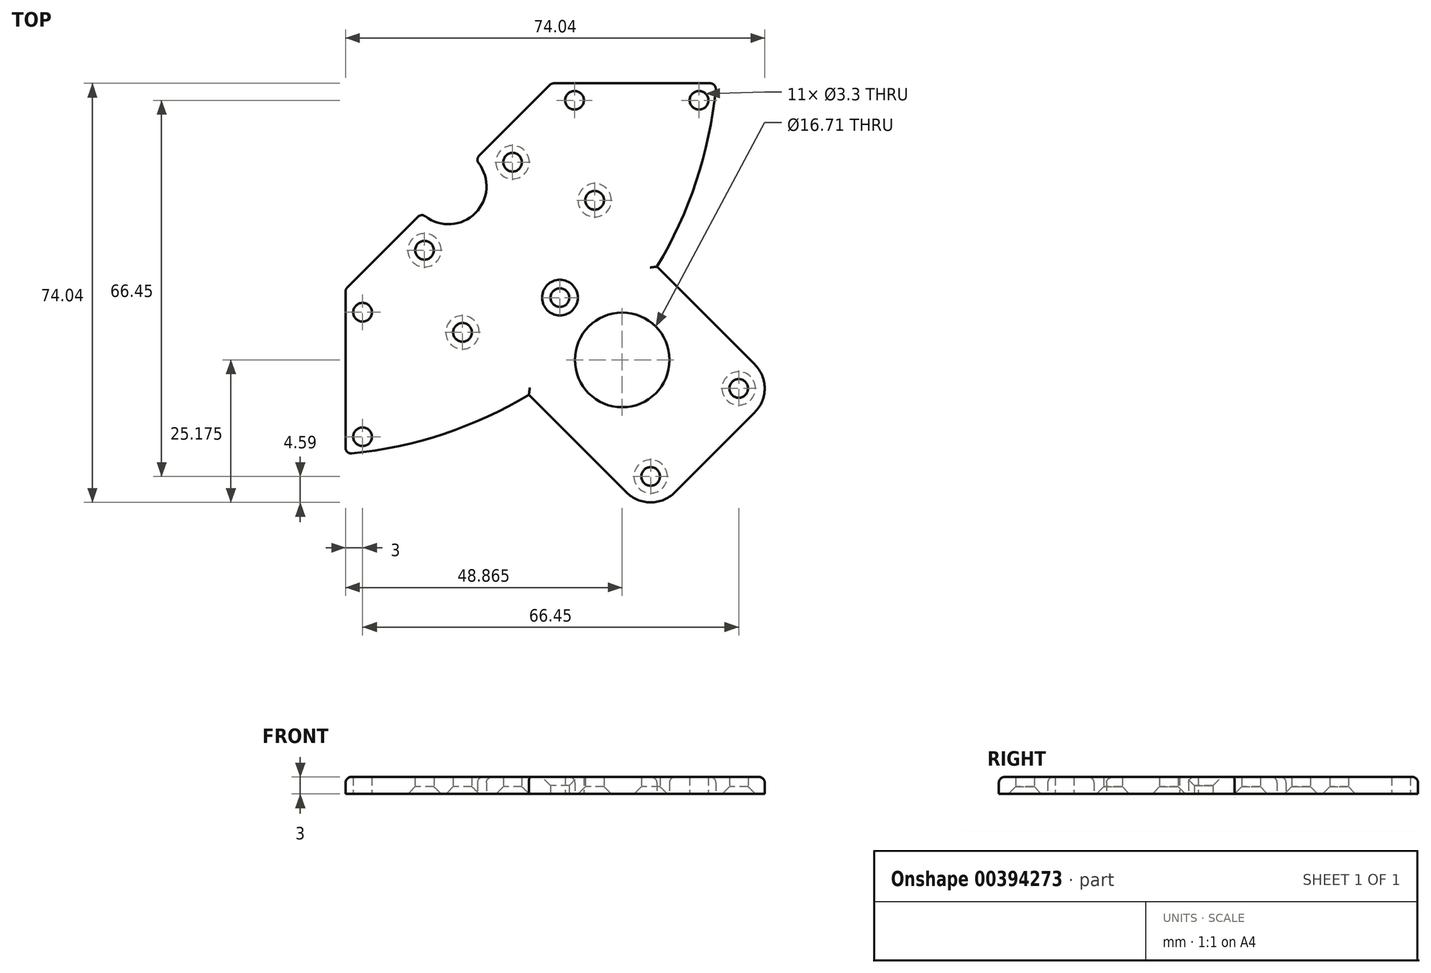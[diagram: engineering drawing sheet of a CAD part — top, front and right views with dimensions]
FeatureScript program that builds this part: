
annotation { "Feature Type Name" : "Feature", "Feature Type Description" : "" }
export const myFeature = defineFeature(function(context is Context, id is Id, definition is map)
    precondition{}
    {
        {
            var Q0;
            Q0=qCreatedBy(makeId("Top.planeOp"),FACE);
            var sketch = newSketch(context, id + "F0", { "sketchPlane" : qUnion([Q0])});
            skCircle(sketch, "E0", {"center": v(49, -11.56) * mm, "radius": 1.65 * mm});
            skCircle(sketch, "E1", {"center": v(71, -11.56) * mm, "radius": 1.65 * mm});
            skLineSegment(sketch, "E2", {"start": v(0, 0) * mm, "end": v(89.43, -89.43) * mm, "construction": true});
            skLineSegment(sketch, "E3", {"start": v(49, -11.56) * mm, "end": v(12.94, -47.62) * mm, "construction": true});
            skCircle(sketch, "E4", {"center": v(38.06, -22.5) * mm, "radius": 1.65 * mm});
            skCircle(sketch, "E5", {"center": v(78, -62.45) * mm, "radius": 1.65 * mm});
            skCircle(sketch, "E6", {"center": v(52.55, -29.22) * mm, "radius": 1.65 * mm});
            skArc(sketch, "E7", {"start": v(63.58, -40.95) * mm, "mid": v(70.67, -25.35) * mm, "end": v(74.06, -8.56) * mm});
            skLineSegment(sketch, "E8", {"start": v(73.77, -73.77) * mm, "end": v(85.08, -62.45) * mm});
            skLineSegment(sketch, "E9", {"start": v(85.08, -62.45) * mm, "end": v(63.58, -40.95) * mm});
            skLineSegment(sketch, "E10", {"start": v(31.49, -22) * mm, "end": v(44.93, -8.56) * mm});
            skLineSegment(sketch, "E11.trimOffspring", {"start": v(44.93, -8.56) * mm, "end": v(74.06, -8.56) * mm});
            skLineSegment(sketch, "E12.MirrorCS", {"start": v(8.56, -44.93) * mm, "end": v(8.56, -74.06) * mm});
            skLineSegment(sketch, "E13.MirrorCS", {"start": v(22, -31.49) * mm, "end": v(8.56, -44.93) * mm});
            skLineSegment(sketch, "E14.MirrorCS", {"start": v(62.45, -85.08) * mm, "end": v(40.95, -63.58) * mm});
            skLineSegment(sketch, "E15.MirrorCS", {"start": v(73.77, -73.77) * mm, "end": v(62.45, -85.08) * mm});
            skArc(sketch, "E16.MirrorCS", {"start": v(40.95, -63.58) * mm, "mid": v(25.35, -70.67) * mm, "end": v(8.56, -74.06) * mm});
            skCircle(sketch, "E17.MirrorC", {"center": v(29.22, -52.55) * mm, "radius": 1.65 * mm});
            skCircle(sketch, "E18.MirrorC", {"center": v(22.5, -38.06) * mm, "radius": 1.65 * mm});
            skCircle(sketch, "E19.MirrorC", {"center": v(11.56, -71) * mm, "radius": 1.65 * mm});
            skCircle(sketch, "E20.MirrorC", {"center": v(62.45, -78) * mm, "radius": 1.65 * mm});
            skCircle(sketch, "E21.MirrorC", {"center": v(11.56, -49) * mm, "radius": 1.65 * mm});
            skArc(sketch, "E22", {"start": v(22, -31.49) * mm, "mid": v(31.49, -31.49) * mm, "end": v(31.49, -22) * mm});
            skCircle(sketch, "E23", {"center": v(57.43, -57.43) * mm, "radius": 8.36 * mm});
            skCircle(sketch, "E24", {"center": v(46.42, -46.42) * mm, "radius": 1.65 * mm});
            skSolve(sketch);
        }
        {
            var Q0;
            Q0 = qSketchRegion(id + "F0", true);
            extrude(context, id + "F1", {"entities" : qUnion([Q0]), "depth" : 3 * mm});
        }
        {
            var Q0;
            Q0=makeQuery(id+"F1.opExtrude","CAP_EDGE",EDGE,{"disambiguationData":[OSD([sQuery(id+"F0.wireOp",EDGE,"E18.MirrorC")])],"isStart":true});
            var Q1;
            Q1=makeQuery(id+"F1.opExtrude","CAP_EDGE",EDGE,{"disambiguationData":[OSD([sQuery(id+"F0.wireOp",EDGE,"E17.MirrorC")])],"isStart":true});
            var Q2;
            Q2=makeQuery(id+"F1.opExtrude","CAP_EDGE",EDGE,{"disambiguationData":[OSD([sQuery(id+"F0.wireOp",EDGE,"E20.MirrorC")])],"isStart":true});
            var Q3;
            Q3=makeQuery(id+"F1.opExtrude","CAP_EDGE",EDGE,{"disambiguationData":[OSD([sQuery(id+"F0.wireOp",EDGE,"E5")])],"isStart":true});
            var Q4;
            Q4=makeQuery(id+"F1.opExtrude","CAP_EDGE",EDGE,{"disambiguationData":[OSD([sQuery(id+"F0.wireOp",EDGE,"E6")])],"isStart":true});
            var Q5;
            Q5=makeQuery(id+"F1.opExtrude","CAP_EDGE",EDGE,{"disambiguationData":[OSD([sQuery(id+"F0.wireOp",EDGE,"E4")])],"isStart":true});
            chamfer(context, id + "F2", {"entities" : qUnion([Q0, Q1, Q2, Q3, Q4, Q5]), "width" : 1.3 * mm, "tangentPropagation" : true});
        }
        {
            var Q0;
            Q0=makeQuery(id+"F1.opExtrude","CAP_EDGE",EDGE,{"disambiguationData":[OSD([sQuery(id+"F0.wireOp",EDGE,"E16.MirrorCS")])],"isStart":false});
            var Q1;
            Q1=makeQuery(id+"F1.opExtrude","CAP_EDGE",EDGE,{"disambiguationData":[OSD([sQuery(id+"F0.wireOp",EDGE,"E14.MirrorCS")])],"isStart":false});
            var Q2;
            Q2=makeQuery(id+"F1.opExtrude","CAP_EDGE",EDGE,{"disambiguationData":[OSD([sQuery(id+"F0.wireOp",EDGE,"E8"),sQuery(id+"F0.wireOp",EDGE,"E15.MirrorCS")])],"isStart":false});
            var Q3;
            Q3=makeQuery(id+"F1.opExtrude","CAP_EDGE",EDGE,{"disambiguationData":[OSD([sQuery(id+"F0.wireOp",EDGE,"E9")])],"isStart":false});
            var Q4;
            Q4=makeQuery(id+"F1.opExtrude","CAP_EDGE",EDGE,{"disambiguationData":[OSD([sQuery(id+"F0.wireOp",EDGE,"E7")])],"isStart":false});
            var Q5;
            Q5=makeQuery(id+"F1.opExtrude","CAP_EDGE",EDGE,{"disambiguationData":[OSD([sQuery(id+"F0.wireOp",EDGE,"E11.trimOffspring")])],"isStart":false});
            var Q6;
            Q6=makeQuery(id+"F1.opExtrude","CAP_EDGE",EDGE,{"disambiguationData":[OSD([sQuery(id+"F0.wireOp",EDGE,"E10")])],"isStart":false});
            var Q7;
            Q7=makeQuery(id+"F1.opExtrude","CAP_EDGE",EDGE,{"disambiguationData":[OSD([sQuery(id+"F0.wireOp",EDGE,"E22")])],"isStart":false});
            var Q8;
            Q8=makeQuery(id+"F1.opExtrude","CAP_EDGE",EDGE,{"disambiguationData":[OSD([sQuery(id+"F0.wireOp",EDGE,"E13.MirrorCS")])],"isStart":false});
            var Q9;
            Q9=makeQuery(id+"F1.opExtrude","CAP_EDGE",EDGE,{"disambiguationData":[OSD([sQuery(id+"F0.wireOp",EDGE,"E12.MirrorCS")])],"isStart":false});
            fillet(context, id + "F3", {"entities" : qUnion([Q0, Q1, Q2, Q3, Q4, Q5, Q6, Q7, Q8, Q9]), "radius" : 1 * mm, "tangentPropagation" : true, "allowEdgeOverflow" : false});
        }
        {
            var Q0;
            Q0=makeQuery(id+"F1.opExtrude","CAP_EDGE",EDGE,{"disambiguationData":[OSD([sQuery(id+"F0.wireOp",EDGE,"E23")])],"isStart":false});
            fillet(context, id + "F4", {"entities" : qUnion([Q0]), "radius" : 1 * mm, "tangentPropagation" : true, "allowEdgeOverflow" : false});
        }
        {
            var Q0;
            Q0=makeQuery(id+"F1.opExtrude","SWEPT_EDGE",EDGE,{"disambiguationData":[OSD([sQuery(id+"F0.wireOp",EDGE,"E14.MirrorCS"),sQuery(id+"F0.wireOp",EDGE,"E15.MirrorCS")])]});
            var Q1;
            Q1=makeQuery(id+"F1.opExtrude","SWEPT_EDGE",EDGE,{"disambiguationData":[OSD([sQuery(id+"F0.wireOp",EDGE,"E8"),sQuery(id+"F0.wireOp",EDGE,"E9")])]});
            fillet(context, id + "F5", {"entities" : qUnion([Q0, Q1]), "radius" : 6 * mm, "tangentPropagation" : true, "allowEdgeOverflow" : false});
        }
        {
            var Q0;
            Q0=makeQuery(id+"F1.opExtrude","SWEPT_EDGE",EDGE,{"disambiguationData":[OSD([sQuery(id+"F0.wireOp",EDGE,"E10"),sQuery(id+"F0.wireOp",EDGE,"E11.trimOffspring")])]});
            var Q1;
            Q1=makeQuery(id+"F1.opExtrude","SWEPT_EDGE",EDGE,{"disambiguationData":[OSD([sQuery(id+"F0.wireOp",EDGE,"E7"),sQuery(id+"F0.wireOp",EDGE,"E11.trimOffspring")])]});
            var Q2;
            Q2=makeQuery(id+"F1.opExtrude","SWEPT_EDGE",EDGE,{"disambiguationData":[OSD([sQuery(id+"F0.wireOp",EDGE,"E10"),sQuery(id+"F0.wireOp",EDGE,"E22")])]});
            var Q3;
            Q3=makeQuery(id+"F1.opExtrude","SWEPT_EDGE",EDGE,{"disambiguationData":[OSD([sQuery(id+"F0.wireOp",EDGE,"E13.MirrorCS"),sQuery(id+"F0.wireOp",EDGE,"E22")])]});
            var Q4;
            Q4=makeQuery(id+"F1.opExtrude","SWEPT_EDGE",EDGE,{"disambiguationData":[OSD([sQuery(id+"F0.wireOp",EDGE,"E12.MirrorCS"),sQuery(id+"F0.wireOp",EDGE,"E13.MirrorCS")])]});
            var Q5;
            Q5=makeQuery(id+"F1.opExtrude","SWEPT_EDGE",EDGE,{"disambiguationData":[OSD([sQuery(id+"F0.wireOp",EDGE,"E12.MirrorCS"),sQuery(id+"F0.wireOp",EDGE,"E16.MirrorCS")])]});
            fillet(context, id + "F6", {"entities" : qUnion([Q0, Q1, Q2, Q3, Q4, Q5]), "radius" : 1 * mm, "tangentPropagation" : true, "allowEdgeOverflow" : false});
        }
        {
            var Q0;
            Q0=makeQuery(id+"F1.opExtrude","CAP_EDGE",EDGE,{"disambiguationData":[OSD([sQuery(id+"F0.wireOp",EDGE,"E24")])],"isStart":false});
            chamfer(context, id + "F7", {"entities" : qUnion([Q0]), "width" : 1.5 * mm, "tangentPropagation" : true});
        }
    });
